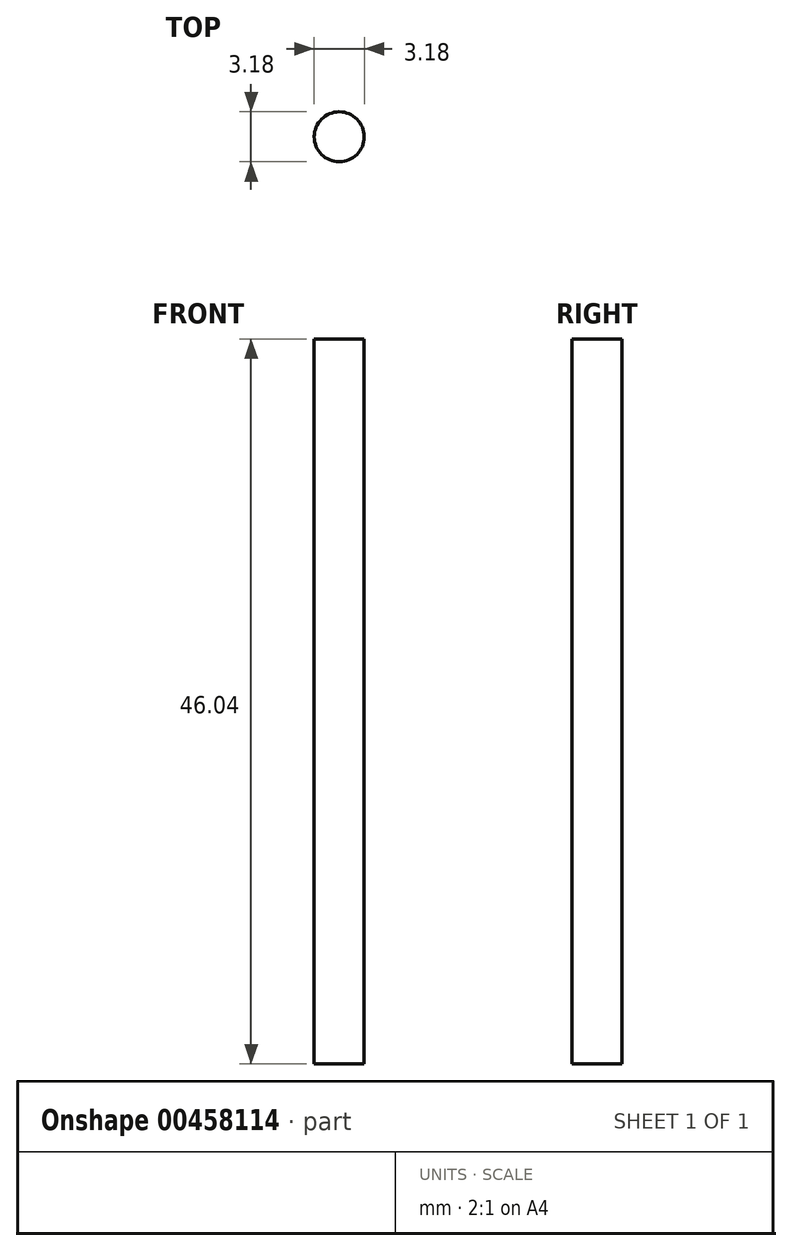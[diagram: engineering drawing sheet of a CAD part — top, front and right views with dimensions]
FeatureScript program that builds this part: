
annotation { "Feature Type Name" : "Feature", "Feature Type Description" : "" }
export const myFeature = defineFeature(function(context is Context, id is Id, definition is map)
    precondition{}
    {
        {
            var Q0;
            Q0=qCreatedBy(makeId("Top.planeOp"),FACE);
            var sketch = newSketch(context, id + "F0", { "sketchPlane" : qUnion([Q0])});
            skCircle(sketch, "E0", {"center": v(0, 0) * mm, "radius": 1.59 * mm});
            skSolve(sketch);
        }
        {
            var Q0;
            Q0=makeQuery(id+"F0.imprint","IMPRINT",FACE,{"disambiguationData":[TD([[makeQuery(id+"F0.imprint","IMPRINT",EDGE,{"derivedFrom":sQuery(id+"F0.wireOp",EDGE,"E0")}),1.0]])]});
            extrude(context, id + "F1", {"entities" : qUnion([Q0]), "depth" : 46.04 * mm});
        }
    });
